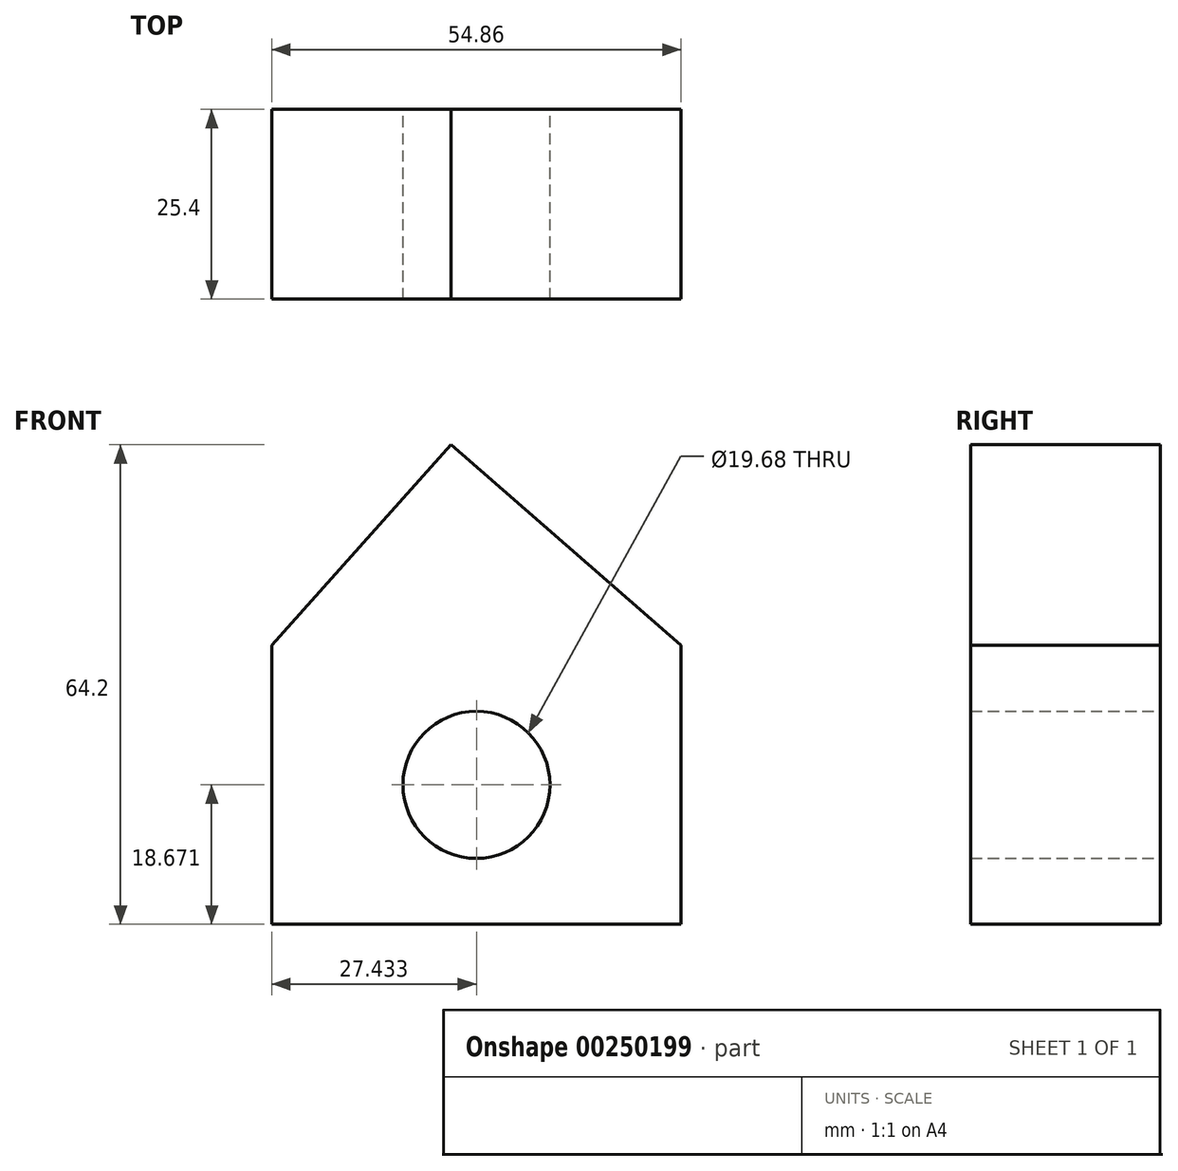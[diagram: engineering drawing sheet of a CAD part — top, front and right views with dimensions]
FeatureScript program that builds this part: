
annotation { "Feature Type Name" : "Feature", "Feature Type Description" : "" }
export const myFeature = defineFeature(function(context is Context, id is Id, definition is map)
    precondition{}
    {
        {
            var Q0;
            Q0=qCreatedBy(makeId("Front.planeOp"),FACE);
            var sketch = newSketch(context, id + "F0", { "sketchPlane" : qUnion([Q0])});
            skLineSegment(sketch, "E0.bottom", {"start": v(-5.72, -3.05) * mm, "end": v(-60.58, -3.05) * mm});
            skLineSegment(sketch, "E0.top", {"start": v(-5.72, 34.3) * mm, "end": v(-60.58, 34.3) * mm});
            skLineSegment(sketch, "E0.left", {"start": v(-5.72, -3.05) * mm, "end": v(-5.72, 34.3) * mm});
            skLineSegment(sketch, "E0.right", {"start": v(-60.58, -3.05) * mm, "end": v(-60.58, 34.3) * mm});
            skPoint(sketch, "E0.middle", {"position": v(-33.15, 15.62) * mm});
            skLineSegment(sketch, "E1", {"start": v(-60.58, 34.3) * mm, "end": v(-36.58, 61.15) * mm});
            skLineSegment(sketch, "E2", {"start": v(-36.58, 61.15) * mm, "end": v(-5.72, 34.3) * mm});
            skCircle(sketch, "E3", {"center": v(-33.15, 15.62) * mm, "radius": 9.84 * mm});
            skSolve(sketch);
        }
        {
            var Q0;
            Q0=makeQuery(id+"F0.imprint","IMPRINT",FACE,{"disambiguationData":[TD([[makeQuery(id+"F0.imprint","IMPRINT",EDGE,{"derivedFrom":sQuery(id+"F0.wireOp",EDGE,"E0.top")}),-1.0]])]});
            var Q1;
            Q1=makeQuery(id+"F0.imprint","IMPRINT",FACE,{"disambiguationData":[TD([[makeQuery(id+"F0.imprint","IMPRINT",EDGE,{"derivedFrom":sQuery(id+"F0.wireOp",EDGE,"E0.bottom")}),-1.0]])]});
            extrude(context, id + "F1", {"entities" : qUnion([Q0, Q1]), "depth" : 25.4 * mm});
        }
    });
